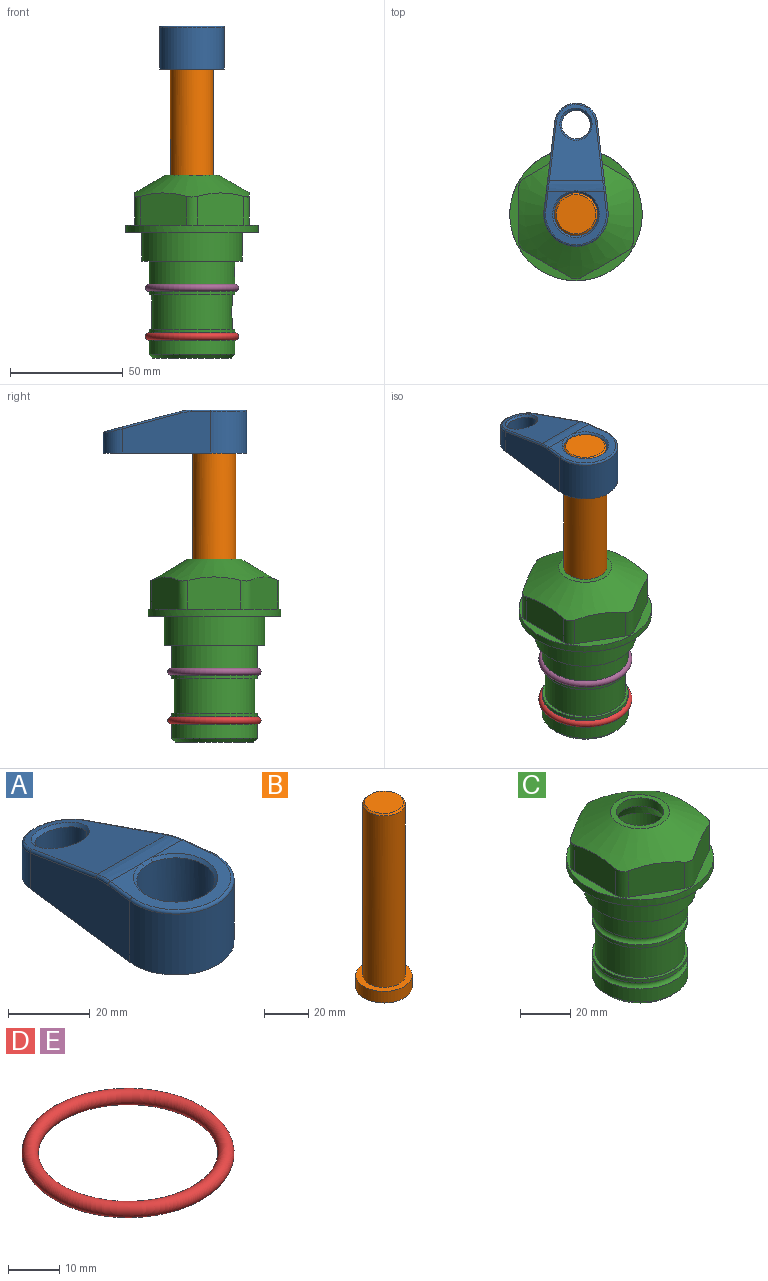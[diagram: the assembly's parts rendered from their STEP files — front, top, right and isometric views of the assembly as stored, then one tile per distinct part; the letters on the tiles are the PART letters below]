
ASSEMBLY  parts=5 mates=4
PART A: 31 faces, bbox 31.7x65.5x19.8 mm
  f0: plane 39.12x18.26mm, normal (0.99,0.12,0), area 612.2mm2, adj f1,f4,f7,f11,f13,f15
  f1: cylinder r=9.53mm len=18.91mm, axis (0,0,-1), area 296.1mm2, adj f0,f2,f7,f17
  f2: plane 39.12x18.26mm, normal (-0.99,0.12,0), area 612.2mm2, adj f1,f4,f7,f12,f14,f16
  f3: cylinder r=6.35mm len=12.7mm, axis (0,0,-1), area 362.4mm2, adj f7,f18
  f4: cylinder r=14.29mm len=28.58mm, axis (0,0,-1), area 882.2mm2, adj f0,f2,f7,f10
  f5: cylinder r=9.53mm len=19.05mm, axis (0,0,-1), area 1092.6mm2, adj f7,f19,f20
  f6: plane 26.99x23.69mm, normal (0,0,1), area 216.2mm2, adj f9,f10,f11,f12,f19
  f7: plane 63.5x28.58mm, normal (0,0,-1), area 661.8mm2, adj f0,f1,f2,f3,f4,f5,f22,f23
  f8: plane 33.52x23.6mm, normal (0,0.26,0.97), area 486mm2, adj f9,f15,f16,f17,f18
  f9: cylinder r=19.05mm len=24.72mm, axis (1,0,0), area 120.4mm2, adj f6,f8,f13,f14,f20
  f10: torus R=13.49mm, axis (0,0,1), area 59mm2, adj f4,f6,f11,f12
  f11: cylinder r=0.79mm len=8.67mm, axis (0.12,-0.99,0), area 10.8mm2, adj f0,f6,f10,f13
  f12: cylinder r=0.79mm len=8.67mm, axis (0.12,0.99,0), area 10.8mm2, adj f2,f6,f10,f14
  f13: bspline ~4.95x1.42mm, area 6.1mm2, adj f0,f9,f11,f15
  f14: bspline ~4.95x1.42mm, area 6.1mm2, adj f2,f9,f12,f16
  f15: cylinder r=0.79mm len=25.95mm, axis (0.12,-0.96,0.26), area 32.9mm2, adj f0,f8,f13,f17
  f16: cylinder r=0.79mm len=25.95mm, axis (0.12,0.96,-0.26), area 32.9mm2, adj f2,f8,f14,f17
  f17: bspline ~18.91x8.38mm, area 30mm2, adj f1,f8,f15,f16
  f18: bspline ~14.29x14.29mm, area 48.3mm2, adj f3,f8
  f19: cone r=9.53mm half-angle=45deg, axis (0,0,1), area 66.5mm2, adj f5,f6,f20
  f20: bspline ~3.22x0.96mm, area 3.5mm2, adj f5,f9,f19
  f21: plane 2.75x2.72mm, normal (0,0,-1), area 2.9mm2, adj f23,f25,f28
  f22: plane 23.05x15.88mm, normal (-0.99,-0.12,0), area 323.6mm2, adj f7,f25,f26,f27,f28,f29
  f23: plane 23.05x15.88mm, normal (0.99,-0.12,0), area 323.6mm2, adj f7,f21,f25,f27,f28,f30
  f24: cylinder r=9.53mm len=10.69mm, axis (0,0,-1), area 114.7mm2, adj f7,f27,f29,f30
  f25: cylinder r=12.7mm len=20.59mm, axis (0,0,-1), area 381.1mm2, adj f7,f21,f22,f23,f26,f28
  f26: plane 2.75x2.72mm, normal (0,0,-1), area 2.9mm2, adj f22,f25,f28
  f27: plane 19.72x18.37mm, normal (0,-0.26,-0.97), area 291.8mm2, adj f22,f23,f24,f28,f29,f30
  f28: cylinder r=15.88mm len=19.92mm, axis (1,0,0), area 54.8mm2, adj f21,f22,f23,f25,f26,f27
  f29: cylinder r=1.59mm len=11mm, axis (0,0,-1), area 34.7mm2, adj f7,f22,f24,f27
  f30: cylinder r=1.59mm len=11mm, axis (0,0,-1), area 34.7mm2, adj f7,f23,f24,f27
PART B: 6 faces, bbox 25.4x25.4x101.6 mm
  f0: plane 17.46x17.46mm, normal (0,0,1), area 239.5mm2, adj f5
  f1: plane 25.4x25.4mm, normal (0,0,-1), area 506.7mm2, adj f2
  f2: cylinder r=12.7mm len=25.4mm, axis (0,0,1), area 506.7mm2, adj f1,f3
  f3: plane 25.4x25.4mm, normal (0,0,1), area 221.7mm2, adj f2,f4
  f4: cylinder r=9.53mm len=94.46mm, axis (0,0,1), area 5653mm2, adj f3,f5
  f5: cone r=8.73mm half-angle=45deg, axis (0,0,-1), area 64.4mm2, adj f0,f4
PART C: 36 faces, bbox 58.7x58.7x81 mm
  f0: cylinder r=17.78mm len=35.56mm, axis (0,0,1), area 1670.8mm2, adj f23,f24,f31
  f1: cylinder r=19.05mm len=38.1mm, axis (0,0,1), area 1191.9mm2, adj f26,f27,f30
  f2: plane 58.66x58.66mm, normal (0,0,-1), area 1150.6mm2, adj f3,f28
  f3: cylinder r=29.33mm len=58.66mm, axis (0,0,-1), area 585.1mm2, adj f2,f4
  f4: plane 58.66x58.66mm, normal (0,0,1), area 475.9mm2, adj f3,f5,f6,f7,f8,f9,f10,f11
  f5: plane 20.32x14.34mm, normal (-0.5,0.87,0), area 324.4mm2, adj f4,f15,f16,f17
  f6: plane 20.32x14.34mm, normal (0.5,0.87,0), area 324.4mm2, adj f4,f14,f15,f17
  f7: plane 23.48x14.34mm, normal (1,0,0), area 324.4mm2, adj f4,f13,f14,f17
  f8: plane 20.32x14.34mm, normal (0.5,-0.87,0), area 324.4mm2, adj f4,f12,f13,f17
  f9: plane 20.32x14.34mm, normal (-0.5,-0.87,0), area 324.4mm2, adj f4,f11,f12,f17
  f10: plane 23.48x14.34mm, normal (-1,0,0), area 324.4mm2, adj f4,f11,f16,f17
  f11: cylinder r=5.08mm len=12.85mm, axis (0,0,-1), area 67.2mm2, adj f4,f9,f10,f17
  f12: cylinder r=5.08mm len=12.85mm, axis (0,0,-1), area 67.2mm2, adj f4,f8,f9,f17
  f13: cylinder r=5.08mm len=12.85mm, axis (0,0,-1), area 67.2mm2, adj f4,f7,f8,f17
  f14: cylinder r=5.08mm len=12.85mm, axis (0,0,-1), area 67.2mm2, adj f4,f6,f7,f17
  f15: cylinder r=5.08mm len=12.85mm, axis (0,0,-1), area 67.2mm2, adj f4,f5,f6,f17
  f16: cylinder r=5.08mm len=12.85mm, axis (0,0,-1), area 67.2mm2, adj f4,f5,f10,f17
  f17: cone r=11.73mm half-angle=60deg, axis (0,0,-1), area 2071.8mm2, adj f5,f6,f7,f8,f9,f10,f11,f12
  f18: plane 23.46x23.46mm, normal (0,0,1), area 147.4mm2, adj f17,f35
  f19: plane 34.93x34.93mm, normal (0,0,-1), area 958mm2, adj f29
  f20: cylinder r=19.05mm len=38.1mm, axis (0,0,1), area 760.1mm2, adj f21,f29
  f21: torus R=19.05mm, axis (0,0,1), area 565.3mm2, adj f20,f22
  f22: cylinder r=19.05mm len=38.1mm, axis (0,0,1), area 190mm2, adj f21,f23
  f23: plane 38.1x38.1mm, normal (0,0,1), area 146.9mm2, adj f0,f22
  f24: plane 38.1x38.1mm, normal (0,0,-1), area 146.9mm2, adj f0,f25
  f25: cylinder r=19.05mm len=38.1mm, axis (0,0,1), area 190mm2, adj f24,f26
  f26: torus R=19.05mm, axis (0,0,1), area 565.3mm2, adj f1,f25
  f27: plane 44.45x44.45mm, normal (0,0,-1), area 411.7mm2, adj f1,f28
  f28: cylinder r=22.23mm len=44.45mm, axis (0,0,1), area 1773.5mm2, adj f2,f27
  f29: cone r=19.05mm half-angle=45deg, axis (0,0,1), area 257.5mm2, adj f19,f20
  f30: cylinder r=3.17mm len=6.75mm, axis (-1,0,0), area 128mm2, adj f1,f33
  f31: cylinder r=3.17mm len=6.35mm, axis (-1,0,0), area 102.5mm2, adj f0,f33
  f32: plane 25.4x25.4mm, normal (0,0,1), area 506.7mm2, adj f33
  f33: cylinder r=12.7mm len=66.42mm, axis (0,0,-1), area 5236.2mm2, adj f30,f31,f32,f34
  f34: cone r=9.53mm half-angle=30deg, axis (0,0,-1), area 443.4mm2, adj f33,f35
  f35: cylinder r=9.53mm len=19.05mm, axis (0,0,-1), area 240.9mm2, adj f18,f34
PART D: 1 faces, bbox 44.7x44.7x3.2 mm
  f0: torus R=19.05mm, axis (0,0,1), area 1193.9mm2
PART E: same geometry as D
PLACE A t=(0,0,27.95)mm
PLACE B t=(0,0,27.55)mm
PLACE C at identity fixed
PLACE D t=(0,0,-21.59)mm
PLACE E at identity
MATE fastened E.f0 <-> C.f0  axis (0,0,1) through (0,0,-24.51)mm
MATE cylindrical B.f2 <-> C.f0  axis (0,0,-1) through (0,0,-10.55)mm
MATE fastened B.f2 <-> A.f4  axis (0,0,1) through (0,0,91.05)mm
MATE fastened D.f0 <-> C.f0  axis (0,0,1) through (0,0,-46.1)mm
